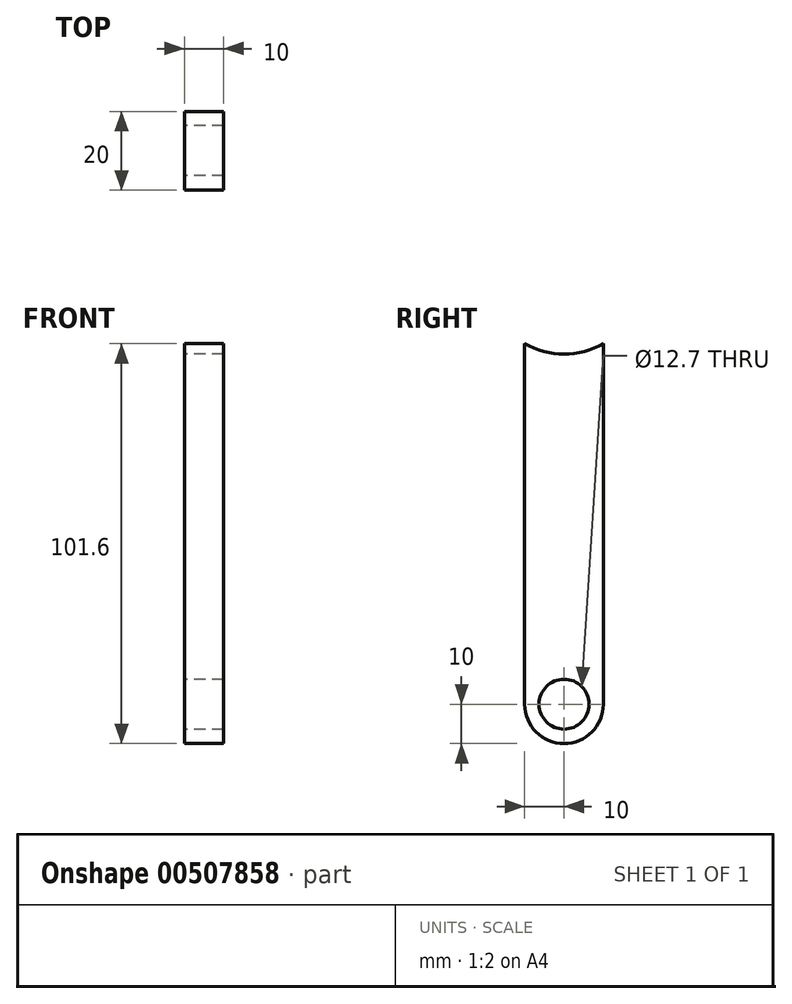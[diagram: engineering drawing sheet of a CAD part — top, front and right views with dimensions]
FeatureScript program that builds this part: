
annotation { "Feature Type Name" : "Feature", "Feature Type Description" : "" }
export const myFeature = defineFeature(function(context is Context, id is Id, definition is map)
    precondition{}
    {
        {
            var Q0;
            Q0=qCreatedBy(makeId("Top.planeOp"),FACE);
            var sketch = newSketch(context, id + "F0", { "sketchPlane" : qUnion([Q0])});
            skLineSegment(sketch, "E0.bottom", {"start": v(0, 0) * mm, "end": v(10, 0) * mm});
            skLineSegment(sketch, "E0.top", {"start": v(0, -20) * mm, "end": v(10, -20) * mm});
            skLineSegment(sketch, "E0.left", {"start": v(0, 0) * mm, "end": v(0, -20) * mm});
            skLineSegment(sketch, "E0.right", {"start": v(10, 0) * mm, "end": v(10, -20) * mm});
            skSolve(sketch);
        }
        {
            var Q0;
            Q0 = qSketchRegion(id + "F0", true);
            extrude(context, id + "F1", {"entities" : qUnion([Q0]), "depth" : 101.6 * mm});
        }
        {
            var Q0;
            Q0=makeQuery(id+"F1.opExtrude","SWEPT_FACE",FACE,{"disambiguationData":[OSD([sQuery(id+"F0.wireOp",EDGE,"E0.left")])]});
            var sketch = newSketch(context, id + "F2", { "sketchPlane" : qUnion([Q0])});
            skCircle(sketch, "E1", {"center": v(10, 10) * mm, "radius": 6.35 * mm});
            skCircle(sketch, "E2", {"center": v(10, 118.92) * mm, "radius": 20 * mm});
            skPoint(sketch, "E2.centerSnap0", {"position": v(10, 101.6) * mm});
            skSolve(sketch);
        }
        {
            var Q0;
            Q0 = qSketchRegion(id + "F2", true);
            extrude(context, id + "F3", {"entities" : qUnion([Q0]), "operationType" : NewBodyOperationType.REMOVE, "oppositeDirection" : true, "depth" : 25.4 * mm});
        }
        {
            var Q0;
            Q0=makeQuery(id+"F1.opExtrude","CAP_EDGE",EDGE,{"disambiguationData":[OSD([sQuery(id+"F0.wireOp",EDGE,"E0.top")])],"isStart":true});
            var Q1;
            Q1=makeQuery(id+"F1.opExtrude","CAP_EDGE",EDGE,{"disambiguationData":[OSD([sQuery(id+"F0.wireOp",EDGE,"E0.bottom")])],"isStart":true});
            fillet(context, id + "F4", {"entities" : qUnion([Q0, Q1]), "radius" : 10 * mm, "tangentPropagation" : true, "allowEdgeOverflow" : false});
        }
    });
